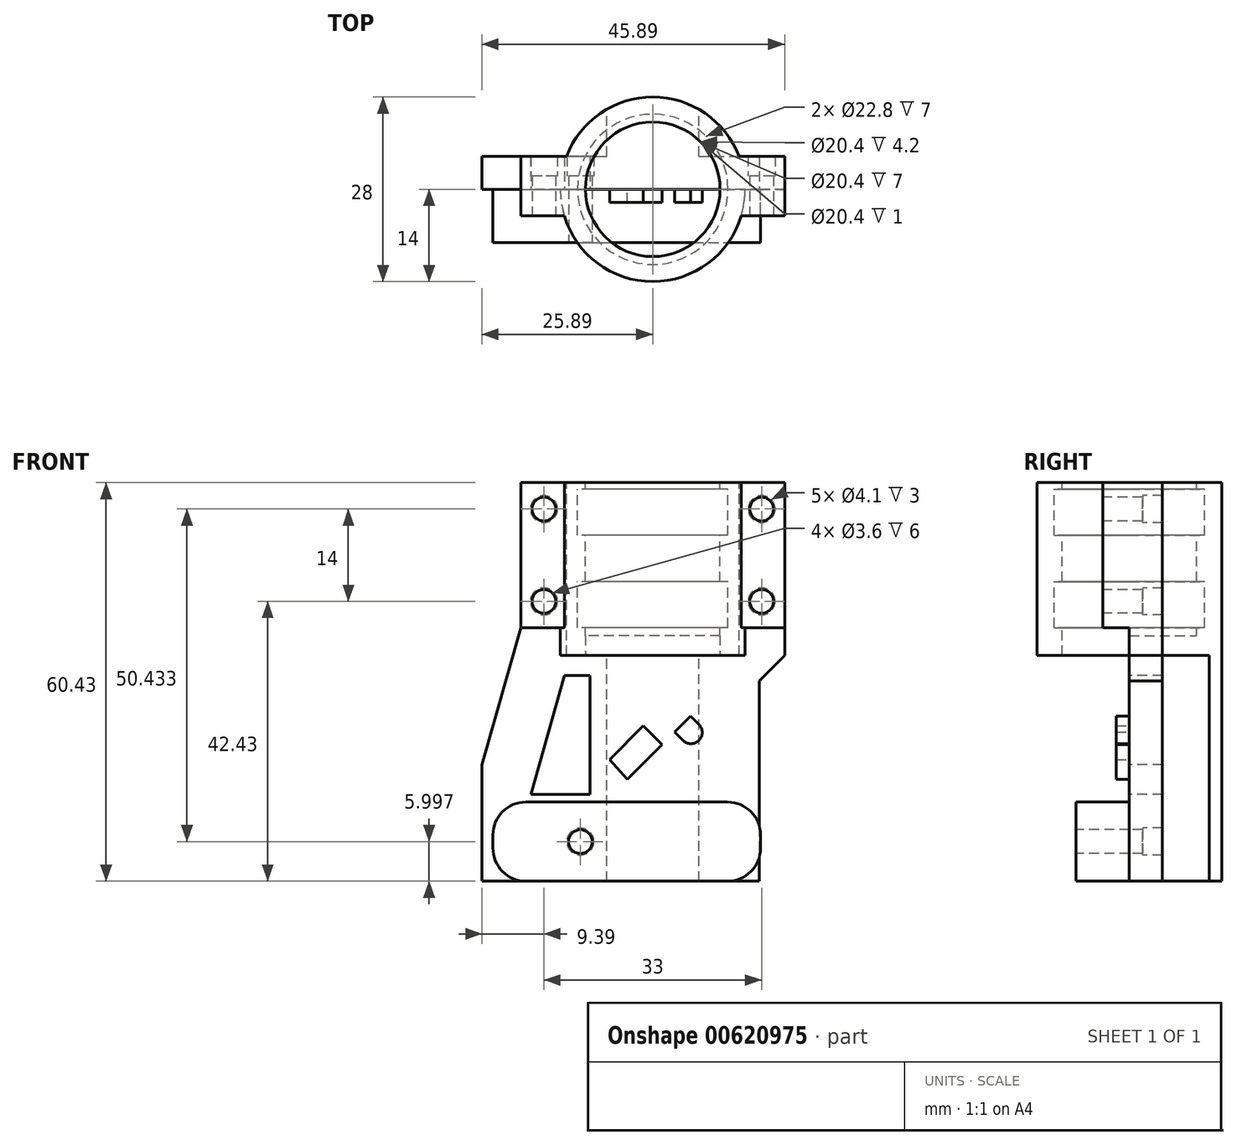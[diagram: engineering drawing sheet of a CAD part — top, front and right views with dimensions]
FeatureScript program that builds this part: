
annotation { "Feature Type Name" : "Feature", "Feature Type Description" : "" }
export const myFeature = defineFeature(function(context is Context, id is Id, definition is map)
    precondition{}
    {
        {
            var Q0;
            Q0=qCreatedBy(makeId("Front.planeOp"),FACE);
            var sketch = newSketch(context, id + "F0", { "sketchPlane" : qUnion([Q0]), "disableImprinting" : false});
            skLineSegment(sketch, "E0", {"start": v(-10.2, 21) * mm, "end": v(-11.4, 21) * mm});
            skLineSegment(sketch, "E1", {"start": v(-11.4, 21) * mm, "end": v(-11.4, 14) * mm});
            skLineSegment(sketch, "E2", {"start": v(-11.4, 14) * mm, "end": v(-10.2, 14) * mm});
            skLineSegment(sketch, "E3", {"start": v(-10.2, 14) * mm, "end": v(-10.2, 7) * mm});
            skLineSegment(sketch, "E4", {"start": v(-10.2, 7) * mm, "end": v(-11.4, 7) * mm});
            skLineSegment(sketch, "E5", {"start": v(-11.4, 7) * mm, "end": v(-11.4, 0) * mm});
            skLineSegment(sketch, "E6", {"start": v(-11.4, 0) * mm, "end": v(-10.2, 0) * mm});
            skLineSegment(sketch, "E7", {"start": v(-10.2, 0) * mm, "end": v(-10.2, -1.2) * mm});
            skLineSegment(sketch, "E8", {"start": v(-10.2, -1.2) * mm, "end": v(0, -1.2) * mm});
            skLineSegment(sketch, "E9", {"start": v(0, -1.2) * mm, "end": v(0, -4.2) * mm});
            skLineSegment(sketch, "E10", {"start": v(0, -4.2) * mm, "end": v(-14, -4.2) * mm});
            skLineSegment(sketch, "E11", {"start": v(-14, -4.2) * mm, "end": v(-14, 22) * mm});
            skLineSegment(sketch, "E12", {"start": v(-14, 22) * mm, "end": v(-10.2, 22) * mm});
            skLineSegment(sketch, "E13", {"start": v(-10.2, 22) * mm, "end": v(-10.2, 21) * mm});
            skLineSegment(sketch, "E14", {"start": v(-10.2, -1.2) * mm, "end": v(-10.2, -4.2) * mm});
            skSolve(sketch);
        }
        {
            var Q0;
            Q0=qSketchRegion(id+"F0",true);
            var Q1;
            Q1=sQuery(id+"F0.wireOp",EDGE,"E9");
            revolve(context, id + "F1", {"entities" : qUnion([Q0]), "axis" : qUnion([Q1]), "revolveType" : RevolveType.ONE_DIRECTION, "angle" : 180 * degree});
        }
        {
            var Q0;
            Q0=makeQuery(id+"F0.imprint","IMPRINT",FACE,{"disambiguationData":[TD([[makeQuery(id+"F0.imprint","IMPRINT",EDGE,{"derivedFrom":sQuery(id+"F0.wireOp",EDGE,"E0")}),-1.0]])]});
            var Q1;
            Q1=sQuery(id+"F0.wireOp",EDGE,"E9");
            revolve(context, id + "F2", {"entities" : qUnion([Q0]), "axis" : qUnion([Q1]), "revolveType" : RevolveType.ONE_DIRECTION, "oppositeDirection" : true, "angle" : 180 * degree});
        }
        {
            var Q0;
            Q0=makeQuery(id+"F1.opRevolve","CAP_FACE",FACE,{"disambiguationData":[OSD([sQuery(id+"F0.wireOp",EDGE,"E0"),sQuery(id+"F0.wireOp",EDGE,"E1"),sQuery(id+"F0.wireOp",EDGE,"E2"),sQuery(id+"F0.wireOp",EDGE,"E3"),sQuery(id+"F0.wireOp",EDGE,"E4"),sQuery(id+"F0.wireOp",EDGE,"E5"),sQuery(id+"F0.wireOp",EDGE,"E6"),sQuery(id+"F0.wireOp",EDGE,"E7"),sQuery(id+"F0.wireOp",EDGE,"E8"),sQuery(id+"F0.wireOp",EDGE,"E9"),sQuery(id+"F0.wireOp",EDGE,"E10"),sQuery(id+"F0.wireOp",EDGE,"E11"),sQuery(id+"F0.wireOp",EDGE,"E12"),sQuery(id+"F0.wireOp",EDGE,"E13")])],"isStart":false});
            var sketch = newSketch(context, id + "F3", { "sketchPlane" : qUnion([Q0])});
            skLineSegment(sketch, "E15.bottom", {"start": v(-11.4, 22) * mm, "end": v(-20, 22) * mm});
            skLineSegment(sketch, "E15.top", {"start": v(-11.4, 0) * mm, "end": v(-20, 0) * mm});
            skLineSegment(sketch, "E15.left", {"start": v(-11.4, 22) * mm, "end": v(-11.4, 0) * mm});
            skLineSegment(sketch, "E15.right", {"start": v(-20, 22) * mm, "end": v(-20, 0) * mm});
            skLineSegment(sketch, "E16", {"start": v(0, 0) * mm, "end": v(0, -4.2) * mm, "construction": true});
            skPoint(sketch, "E17", {"position": v(-16.5, 18) * mm});
            skPoint(sketch, "E17.positionSnap0", {"position": v(-16.5, 22) * mm});
            skPoint(sketch, "E18", {"position": v(-16.5, 4) * mm});
            skPoint(sketch, "E19.MirrorP", {"position": v(16.5, 4) * mm});
            skPoint(sketch, "E20.MirrorP", {"position": v(16.5, 18) * mm});
            skLineSegment(sketch, "E21.MirrorCS", {"start": v(20, 22) * mm, "end": v(20, 0) * mm});
            skLineSegment(sketch, "E22.MirrorCS", {"start": v(11.4, 22) * mm, "end": v(11.4, 0) * mm});
            skLineSegment(sketch, "E23.MirrorCS", {"start": v(11.4, 0) * mm, "end": v(20, 0) * mm});
            skLineSegment(sketch, "E24.MirrorCS", {"start": v(11.4, 22) * mm, "end": v(20, 22) * mm});
            skLineSegment(sketch, "E25.bottom", {"start": v(20, 0) * mm, "end": v(12.54, 0) * mm});
            skLineSegment(sketch, "E25.top", {"start": v(20, -4.2) * mm, "end": v(12.54, -4.2) * mm});
            skLineSegment(sketch, "E25.left", {"start": v(20, 0) * mm, "end": v(20, -4.2) * mm});
            skLineSegment(sketch, "E25.right", {"start": v(12.54, 0) * mm, "end": v(12.54, -4.2) * mm});
            skSolve(sketch);
        }
        {
            var Q0;
            Q0=qSketchRegion(id+"F3",true);
            extrude(context, id + "F4", {"entities" : qUnion([Q0]), "operationType" : NewBodyOperationType.ADD, "flatOperationType" : FlatOperationType.REMOVE, "thickness1" : 5 * mm, "thickness2" : 0 * mm, "thickness" : 5 * mm, "oppositeDirection" : true, "depth" : 5 * mm, "offsetDistance" : 25 * mm, "startOffsetBound" : StartOffsetType.BLIND, "startOffsetDistance" : 25 * mm, "domain" : OperationDomain.MODEL});
        }
        {
            var Q0;
            {var subQ3=sQuery(id+"F3.wireOp",EDGE,"E15.right");Q0=makeQuery(id+"F3.imprint","IMPRINT",FACE,{"disambiguationData":[TD([[makeQuery(id+"F3.imprint","IMPRINT",EDGE,{"derivedFrom":subQ3}),1.0]])]});}
            var Q1;
            {var subQ0=sQuery(id+"F3.wireOp",EDGE,"E21.MirrorCS");Q1=makeQuery(id+"F3.imprint","IMPRINT",FACE,{"disambiguationData":[TD([[makeQuery(id+"F3.imprint","IMPRINT",EDGE,{"derivedFrom":subQ0}),-1.0]])]});}
            var Q2;
            {var subQ0=sQuery(id+"F3.wireOp",EDGE,"E15.left");var subQ1=makeQuery(id+"F3.imprint","INTERSECT",VERTEX,{"derivedFrom":[makeQuery(id+"F1.opRevolve","CAP_EDGE",EDGE,{"disambiguationData":[OSD([sQuery(id+"F0.wireOp",EDGE,"E2")])],"isStart":true}),subQ0]});Q2=makeQuery(id+"F3.imprint","IMPRINT",FACE,{"disambiguationData":[TD([[makeQuery(id+"F3.imprint","IMPRINT",EDGE,{"disambiguationData":[TD([[subQ1,-1.0]])],"derivedFrom":subQ0}),-1.0]])]});}
            var Q3;
            {var subQ0=sQuery(id+"F3.wireOp",EDGE,"E22.MirrorCS");var subQ2=makeQuery(id+"F3.imprint","INTERSECT",VERTEX,{"derivedFrom":[makeQuery(id+"F1.opRevolve","CAP_EDGE",EDGE,{"disambiguationData":[OSD([sQuery(id+"F0.wireOp",EDGE,"E2")])],"isStart":false}),subQ0]});Q3=makeQuery(id+"F3.imprint","IMPRINT",FACE,{"disambiguationData":[TD([[makeQuery(id+"F3.imprint","IMPRINT",EDGE,{"disambiguationData":[TD([[subQ2,-1.0]])],"derivedFrom":subQ0}),1.0]])]});}
            extrude(context, id + "F5", {"entities" : qUnion([Q0, Q1, Q2, Q3]), "operationType" : NewBodyOperationType.ADD, "flatOperationType" : FlatOperationType.REMOVE, "thickness1" : 5 * mm, "thickness2" : 0 * mm, "thickness" : 5 * mm, "depth" : 4 * mm, "offsetDistance" : 25 * mm, "startOffsetBound" : StartOffsetType.BLIND, "startOffsetDistance" : 25 * mm, "domain" : OperationDomain.MODEL});
        }
        {
            var Q0;
            Q0=makeQuery(id+"F4.opExtrude","CAP_FACE",FACE,{"disambiguationData":[OSD([sQuery(id+"F3.wireOp",EDGE,"E21.MirrorCS"),sQuery(id+"F3.wireOp",EDGE,"E22.MirrorCS"),sQuery(id+"F3.wireOp",EDGE,"E23.MirrorCS"),sQuery(id+"F3.wireOp",EDGE,"E24.MirrorCS")])],"isStart":false});
            var sketch = newSketch(context, id + "F6", { "sketchPlane" : qUnion([Q0])});
            skPoint(sketch, "E26.0", {"position": v(-16.5, 18) * mm});
            skPoint(sketch, "E26.1", {"position": v(-16.5, 4) * mm});
            skPoint(sketch, "E26.2", {"position": v(16.5, 4) * mm});
            skPoint(sketch, "E26.3", {"position": v(16.5, 18) * mm});
            skSolve(sketch);
        }
        {
            var Q0;
            Q0=sQuery(id+"F6.wireOp",VERTEX,"E26.0");
            var Q1;
            Q1=sQuery(id+"F6.wireOp",VERTEX,"E26.1");
            var Q2;
            Q2=sQuery(id+"F6.wireOp",VERTEX,"E26.3");
            var Q3;
            Q3=sQuery(id+"F6.wireOp",VERTEX,"E26.2");
            var Q4;
            Q4=makeQuery(id+"F1.opRevolve","SWEPT_BODY",BODY,{"disambiguationData":[OSD([sQuery(id+"F0.wireOp",EDGE,"E0"),sQuery(id+"F0.wireOp",EDGE,"E1"),sQuery(id+"F0.wireOp",EDGE,"E2"),sQuery(id+"F0.wireOp",EDGE,"E3"),sQuery(id+"F0.wireOp",EDGE,"E4"),sQuery(id+"F0.wireOp",EDGE,"E5"),sQuery(id+"F0.wireOp",EDGE,"E6"),sQuery(id+"F0.wireOp",EDGE,"E7"),sQuery(id+"F0.wireOp",EDGE,"E8"),sQuery(id+"F0.wireOp",EDGE,"E9"),sQuery(id+"F0.wireOp",EDGE,"E10"),sQuery(id+"F0.wireOp",EDGE,"E11"),sQuery(id+"F0.wireOp",EDGE,"E12"),sQuery(id+"F0.wireOp",EDGE,"E13")])]});
            var Q5;
            Q5=makeQuery(id+"F2.opRevolve","SWEPT_BODY",BODY,{"disambiguationData":[OSD([sQuery(id+"F0.wireOp",EDGE,"E0"),sQuery(id+"F0.wireOp",EDGE,"E1"),sQuery(id+"F0.wireOp",EDGE,"E2"),sQuery(id+"F0.wireOp",EDGE,"E3"),sQuery(id+"F0.wireOp",EDGE,"E4"),sQuery(id+"F0.wireOp",EDGE,"E5"),sQuery(id+"F0.wireOp",EDGE,"E6"),sQuery(id+"F0.wireOp",EDGE,"E7"),sQuery(id+"F0.wireOp",EDGE,"E8"),sQuery(id+"F0.wireOp",EDGE,"E9"),sQuery(id+"F0.wireOp",EDGE,"E10"),sQuery(id+"F0.wireOp",EDGE,"E11"),sQuery(id+"F0.wireOp",EDGE,"E12"),sQuery(id+"F0.wireOp",EDGE,"E13")])]});
            hole(context, id + "F7", {"style" : HoleStyle.C_BORE, "endStyle" : HoleEndStyle.THROUGH, "holeDiameter" : 3.6 * mm, "cBoreDiameter" : 4.1 * mm, "cBoreDepth" : 3 * mm, "majorDiameter" : 5 * mm, "isTappedThrough" : true, "tappedDepth" : 7 * mm, "tapClearance" : 6, "locations" : qUnion([Q0, Q1, Q2, Q3]), "scope" : qUnion([Q4, Q5]), "startStyle" : HoleStartStyle.SKETCH});
        }
        {
            var Q0;
            Q0=qCreatedBy(makeId("Front.planeOp"),FACE);
            var sketch = newSketch(context, id + "F8", { "sketchPlane" : qUnion([Q0])});
            skLineSegment(sketch, "E27", {"start": v(0, 7.53) * mm, "end": v(0, -50) * mm, "construction": true});
            skLineSegment(sketch, "E28", {"start": v(-3.83, -22.95) * mm, "end": v(17.38, -1.74) * mm, "construction": true});
            skLineSegment(sketch, "E29", {"start": v(-1, -47) * mm, "end": v(41.43, -4.56) * mm, "construction": true});
            skLineSegment(sketch, "E30", {"start": v(20.21, -25.78) * mm, "end": v(5.8, -11.37) * mm, "construction": true});
            skLineSegment(sketch, "E31", {"start": v(17.38, -1.74) * mm, "end": v(41.43, -4.56) * mm, "construction": true});
            skLineSegment(sketch, "E32", {"start": v(-3.83, -22.95) * mm, "end": v(-1, -47) * mm, "construction": true});
            skLineSegment(sketch, "E33", {"start": v(5.72, -13.4) * mm, "end": v(7, -14.68) * mm, "construction": true});
            skLineSegment(sketch, "E34", {"start": v(3.31, -15.8) * mm, "end": v(4.59, -17.08) * mm, "construction": true});
            skArc(sketch, "E35", {"start": v(4.59, -17.08) * mm, "mid": v(7, -17.08) * mm, "end": v(7, -14.68) * mm});
            skPoint(sketch, "E36", {"position": v(7, -17.08) * mm});
            skSolve(sketch);
        }
        {
            var Q0;
            Q0=makeQuery(id+"F0.imprint","IMPRINT",FACE,{"disambiguationData":[TD([[makeQuery(id+"F0.imprint","IMPRINT",EDGE,{"derivedFrom":sQuery(id+"F0.wireOp",EDGE,"E0")}),-1.0]])]});
            var sketch = newSketch(context, id + "F9", { "sketchPlane" : qUnion([Q0])});
            skLineSegment(sketch, "E37.top", {"start": v(-25.9, -38.43) * mm, "end": v(16.16, -38.43) * mm});
            skLineSegment(sketch, "E37.left", {"start": v(-25.9, -20.76) * mm, "end": v(-25.9, -38.43) * mm});
            skLineSegment(sketch, "E37.right", {"start": v(16.16, -8.04) * mm, "end": v(16.16, -38.43) * mm});
            skArc(sketch, "E38.0", {"start": v(4.59, -17.08) * mm, "mid": v(7, -17.08) * mm, "end": v(7, -14.68) * mm});
            skLineSegment(sketch, "E38.1", {"start": v(3.31, -15.8) * mm, "end": v(4.59, -17.08) * mm});
            skLineSegment(sketch, "E38.2", {"start": v(5.72, -13.4) * mm, "end": v(7, -14.68) * mm});
            skLineSegment(sketch, "E38.3", {"start": v(-3.83, -22.95) * mm, "end": v(1.4, -17.72) * mm});
            skLineSegment(sketch, "E39", {"start": v(-3.85, -22.97) * mm, "end": v(1.4, -17.72) * mm});
            skLineSegment(sketch, "E40", {"start": v(1.4, -17.72) * mm, "end": v(-1.42, -14.89) * mm});
            skLineSegment(sketch, "E41", {"start": v(-1.42, -14.89) * mm, "end": v(-6.53, -20) * mm});
            skLineSegment(sketch, "E42", {"start": v(-6.53, -20) * mm, "end": v(-3.85, -22.97) * mm});
            skLineSegment(sketch, "E43", {"start": v(-20, 0) * mm, "end": v(-25.9, -20.76) * mm});
            skLineSegment(sketch, "E44", {"start": v(-9.49, -7.27) * mm, "end": v(-9.49, -25.26) * mm});
            skLineSegment(sketch, "E45", {"start": v(-9.49, -25.26) * mm, "end": v(-18.46, -25.26) * mm});
            skLineSegment(sketch, "E46", {"start": v(-18.46, -25.26) * mm, "end": v(-13.36, -7.27) * mm});
            skPoint(sketch, "E47.0", {"position": v(-20, 0) * mm});
            skLineSegment(sketch, "E48", {"start": v(-13.36, -7.27) * mm, "end": v(-9.49, -7.27) * mm});
            skLineSegment(sketch, "E49", {"start": v(20, -4.2) * mm, "end": v(16.16, -8.04) * mm});
            skPoint(sketch, "E50.orphan", {"position": v(17.38, -1.74) * mm});
            skLineSegment(sketch, "E51.trimOffspring", {"start": v(3.31, -15.8) * mm, "end": v(5.72, -13.4) * mm});
            skLineSegment(sketch, "E52", {"start": v(20, -4.2) * mm, "end": v(-10.89, -4.2) * mm});
            skLineSegment(sketch, "E53", {"start": v(-10.89, -4.2) * mm, "end": v(-10.89, 0) * mm});
            skLineSegment(sketch, "E54", {"start": v(-10.89, 0) * mm, "end": v(-20, 0) * mm});
            skSolve(sketch);
        }
        {
            var Q0;
            {var subQ5=sQuery(id+"F9.wireOp",EDGE,"E53");Q0=makeQuery(id+"F9.imprint","IMPRINT",FACE,{"disambiguationData":[TD([[makeQuery(id+"F9.imprint","IMPRINT",EDGE,{"derivedFrom":subQ5}),1.0]])]});}
            var Q1;
            Q1=makeQuery(id+"F9.imprint","IMPRINT",FACE,{"disambiguationData":[TD([[makeQuery(id+"F9.imprint","IMPRINT",EDGE,{"derivedFrom":sQuery(id+"F9.wireOp",EDGE,"E37.top")}),1.0]])]});
            var Q2;
            Q2=makeQuery(id+"F9.imprint","IMPRINT",FACE,{"disambiguationData":[TD([[makeQuery(id+"F9.imprint","IMPRINT",EDGE,{"derivedFrom":sQuery(id+"F9.wireOp",EDGE,"E38.0")}),1.0]])]});
            var Q3;
            {var subQ0=sQuery(id+"F9.wireOp",EDGE,"E40");Q3=makeQuery(id+"F9.imprint","IMPRINT",FACE,{"disambiguationData":[TD([[makeQuery(id+"F9.imprint","IMPRINT",EDGE,{"derivedFrom":subQ0}),1.0]])]});}
            extrude(context, id + "F10", {"entities" : qUnion([Q0, Q1, Q2, Q3]), "operationType" : NewBodyOperationType.ADD, "thickness1" : 5 * mm, "thickness2" : 0 * mm, "thickness" : 5 * mm, "oppositeDirection" : true, "depth" : 5 * mm, "offsetDistance" : 25 * mm, "startOffsetBound" : StartOffsetType.BLIND, "startOffsetDistance" : 25 * mm, "flatOperationType" : FlatOperationType.REMOVE, "domain" : OperationDomain.MODEL});
        }
        {
            var Q0;
            Q0=makeQuery(id+"F9.imprint","IMPRINT",FACE,{"disambiguationData":[TD([[makeQuery(id+"F9.imprint","IMPRINT",EDGE,{"derivedFrom":sQuery(id+"F9.wireOp",EDGE,"E39")}),1.0]])]});
            var Q1;
            Q1=makeQuery(id+"F9.imprint","IMPRINT",FACE,{"disambiguationData":[TD([[makeQuery(id+"F9.imprint","IMPRINT",EDGE,{"derivedFrom":sQuery(id+"F9.wireOp",EDGE,"E38.0")}),1.0]])]});
            extrude(context, id + "F11", {"entities" : qUnion([Q0, Q1]), "operationType" : NewBodyOperationType.ADD, "depth" : 2 * mm, "offsetDistance" : 25 * mm});
        }
        {
            var Q0;
            Q0=makeQuery(id+"F10.boolean.opBoolean","MERGE",FACE,{"derivedFrom":[makeQuery(id+"F4.boolean.opBoolean","MERGE",FACE,{"derivedFrom":[makeQuery(id+"F1.opRevolve","CAP_FACE",FACE,{"disambiguationData":[OSD([sQuery(id+"F0.wireOp",EDGE,"E0"),sQuery(id+"F0.wireOp",EDGE,"E1"),sQuery(id+"F0.wireOp",EDGE,"E2"),sQuery(id+"F0.wireOp",EDGE,"E3"),sQuery(id+"F0.wireOp",EDGE,"E4"),sQuery(id+"F0.wireOp",EDGE,"E5"),sQuery(id+"F0.wireOp",EDGE,"E6"),sQuery(id+"F0.wireOp",EDGE,"E7"),sQuery(id+"F0.wireOp",EDGE,"E8"),sQuery(id+"F0.wireOp",EDGE,"E9"),sQuery(id+"F0.wireOp",EDGE,"E10"),sQuery(id+"F0.wireOp",EDGE,"E11"),sQuery(id+"F0.wireOp",EDGE,"E12"),sQuery(id+"F0.wireOp",EDGE,"E13")])],"isStart":false}),makeQuery(id+"F4.opExtrude","CAP_FACE",FACE,{"disambiguationData":[OSD([sQuery(id+"F3.wireOp",EDGE,"E15.bottom"),sQuery(id+"F3.wireOp",EDGE,"E15.top"),sQuery(id+"F3.wireOp",EDGE,"E15.left"),sQuery(id+"F3.wireOp",EDGE,"E15.right")])],"isStart":true}),makeQuery(id+"F4.opExtrude","CAP_FACE",FACE,{"disambiguationData":[OSD([sQuery(id+"F3.wireOp",EDGE,"E21.MirrorCS"),sQuery(id+"F3.wireOp",EDGE,"E22.MirrorCS"),sQuery(id+"F3.wireOp",EDGE,"E23.MirrorCS"),sQuery(id+"F3.wireOp",EDGE,"E24.MirrorCS")])],"isStart":true})]}),makeQuery(id+"F10.opExtrude","CAP_FACE",FACE,{"disambiguationData":[OSD([sQuery(id+"F9.wireOp",EDGE,"E37.top"),sQuery(id+"F9.wireOp",EDGE,"E37.left"),sQuery(id+"F9.wireOp",EDGE,"E37.right"),sQuery(id+"F9.wireOp",EDGE,"sIr9ozcs-yVTk-N2fr-iWXJ-KNAt2VVmV1aQ")])],"isStart":true})]});
            var sketch = newSketch(context, id + "F12", { "sketchPlane" : qUnion([Q0]), "disableImprinting" : false});
            skLineSegment(sketch, "E55.bottom", {"start": v(-24.23, -26.43) * mm, "end": v(16.34, -26.43) * mm});
            skLineSegment(sketch, "E55.top", {"start": v(-24.23, -38.43) * mm, "end": v(16.34, -38.43) * mm});
            skLineSegment(sketch, "E55.left", {"start": v(-24.23, -26.43) * mm, "end": v(-24.23, -38.43) * mm});
            skLineSegment(sketch, "E55.right", {"start": v(16.34, -26.43) * mm, "end": v(16.34, -38.43) * mm});
            skPoint(sketch, "E56", {"position": v(-10.97, -32.43) * mm});
            skPoint(sketch, "E56.positionSnap0", {"position": v(-24.23, -32.43) * mm});
            skSolve(sketch);
        }
        {
            var Q0;
            Q0=makeQuery(id+"F12.imprint","IMPRINT",FACE,{"disambiguationData":[TD([[makeQuery(id+"F12.imprint","IMPRINT",EDGE,{"derivedFrom":sQuery(id+"F12.wireOp",EDGE,"E55.bottom")}),-1.0]])]});
            extrude(context, id + "F13", {"entities" : qUnion([Q0]), "depth" : 8.1 * mm, "offsetDistance" : 25 * mm});
        }
        {
            var Q0;
            Q0=makeQuery(id+"F10.boolean.opBoolean","MERGE",FACE,{"derivedFrom":[makeQuery(id+"F4.opExtrude","CAP_FACE",FACE,{"disambiguationData":[OSD([sQuery(id+"F3.wireOp",EDGE,"E21.MirrorCS"),sQuery(id+"F3.wireOp",EDGE,"E22.MirrorCS"),sQuery(id+"F3.wireOp",EDGE,"E23.MirrorCS"),sQuery(id+"F3.wireOp",EDGE,"E24.MirrorCS"),sQuery(id+"F3.wireOp",EDGE,"E25.top"),sQuery(id+"F3.wireOp",EDGE,"E25.left"),sQuery(id+"F3.wireOp",EDGE,"E25.right")])],"isStart":false}),makeQuery(id+"F4.opExtrude","CAP_FACE",FACE,{"disambiguationData":[OSD([sQuery(id+"F3.wireOp",EDGE,"E15.bottom"),sQuery(id+"F3.wireOp",EDGE,"E15.top"),sQuery(id+"F3.wireOp",EDGE,"E15.left"),sQuery(id+"F3.wireOp",EDGE,"E15.right")])],"isStart":false}),makeQuery(id+"F10.opExtrude","CAP_FACE",FACE,{"disambiguationData":[OSD([sQuery(id+"F9.wireOp",EDGE,"E37.top"),sQuery(id+"F9.wireOp",EDGE,"E37.left"),sQuery(id+"F9.wireOp",EDGE,"E37.right"),sQuery(id+"F9.wireOp",EDGE,"E43"),sQuery(id+"F9.wireOp",EDGE,"E44"),sQuery(id+"F9.wireOp",EDGE,"E45"),sQuery(id+"F9.wireOp",EDGE,"E46"),sQuery(id+"F9.wireOp",EDGE,"E48"),sQuery(id+"F9.wireOp",EDGE,"E49"),sQuery(id+"F9.wireOp",EDGE,"E52"),sQuery(id+"F9.wireOp",EDGE,"E53"),sQuery(id+"F9.wireOp",EDGE,"E54")])],"isStart":false})]});
            var sketch = newSketch(context, id + "F14", { "sketchPlane" : qUnion([Q0]), "disableImprinting" : false});
            skPoint(sketch, "E57.0", {"position": v(10.97, -32.43) * mm});
            skSolve(sketch);
        }
        {
            var Q0;
            Q0=sQuery(id+"F14.wireOp",VERTEX,"E57.0");
            var Q1;
            Q1=makeQuery(id+"F13.opExtrude","SWEPT_BODY",BODY,{"disambiguationData":[OSD([sQuery(id+"F12.wireOp",EDGE,"E55.bottom"),sQuery(id+"F12.wireOp",EDGE,"E55.top"),sQuery(id+"F12.wireOp",EDGE,"E55.left"),sQuery(id+"F12.wireOp",EDGE,"E55.right")])]});
            var Q2;
            Q2=makeQuery(id+"F1.opRevolve","SWEPT_BODY",BODY,{"disambiguationData":[OSD([sQuery(id+"F0.wireOp",EDGE,"E0"),sQuery(id+"F0.wireOp",EDGE,"E1"),sQuery(id+"F0.wireOp",EDGE,"E2"),sQuery(id+"F0.wireOp",EDGE,"E3"),sQuery(id+"F0.wireOp",EDGE,"E4"),sQuery(id+"F0.wireOp",EDGE,"E5"),sQuery(id+"F0.wireOp",EDGE,"E6"),sQuery(id+"F0.wireOp",EDGE,"E7"),sQuery(id+"F0.wireOp",EDGE,"E8"),sQuery(id+"F0.wireOp",EDGE,"E9"),sQuery(id+"F0.wireOp",EDGE,"E10"),sQuery(id+"F0.wireOp",EDGE,"E11"),sQuery(id+"F0.wireOp",EDGE,"E12"),sQuery(id+"F0.wireOp",EDGE,"E13")])]});
            hole(context, id + "F15", {"style" : HoleStyle.C_BORE, "endStyle" : HoleEndStyle.THROUGH, "offsetDistance" : 5 * mm, "threadStandard" : ThreadStandard.UNSET, "ansiThreadClass" : lookupTablePath({ "class" : "2B" }), "isoThreadClass" : lookupTablePath({ "class" : "6H" }), "holeDiameter" : 3.6 * mm, "holeDiameterToleranceType" : ToleranceTypeExtended.NONE, "holeDiameterToleranceBoundSymmetrical" : 0.1 * mm, "holeDiameterToleranceBoundDeviationUpper" : 0.1 * mm, "holeDiameterToleranceBoundDeviationLower" : -0.1 * mm, "holeDiameterToleranceBoundLimitsUpper" : 0.1 * mm, "holeDiameterToleranceBoundLimitsLower" : -0.1 * mm, "holeDiameterFitToleranceTable" : lookupTablePath({ "fit" : "User defined", "standard" : "ISO", "shaftClass" : "None", "holeClass" : "A9" }), "holeDiameterholeClassToleranceBoundLimitsUpper" : 0.1 * mm, "holeDiameterholeClassToleranceBoundLimitsLower" : -0.1 * mm, "cBoreDiameter" : 4.1 * mm, "cBoreDiameterToleranceType" : ToleranceType.NONE, "cBoreDiameterToleranceBoundSymmetrical" : 0.1 * mm, "cBoreDiameterToleranceBoundDeviationUpper" : 0.1 * mm, "cBoreDiameterToleranceBoundDeviationLower" : -0.1 * mm, "cBoreDiameterToleranceBoundLimitsUpper" : 0.1 * mm, "cBoreDiameterToleranceBoundLimitsLower" : -0.1 * mm, "cBoreDepth" : 3 * mm, "cBoreDepthToleranceType" : ToleranceType.NONE, "cBoreDepthToleranceBoundSymmetrical" : 0.1 * mm, "cBoreDepthToleranceBoundDeviationUpper" : 0.1 * mm, "cBoreDepthToleranceBoundDeviationLower" : -0.1 * mm, "cBoreDepthToleranceBoundLimitsUpper" : 0.1 * mm, "cBoreDepthToleranceBoundLimitsLower" : -0.1 * mm, "cSinkDiameterToleranceType" : ToleranceType.NONE, "cSinkDiameterToleranceBoundSymmetrical" : 0.1 * mm, "cSinkDiameterToleranceBoundDeviationUpper" : 0.1 * mm, "cSinkDiameterToleranceBoundDeviationLower" : -0.1 * mm, "cSinkDiameterToleranceBoundLimitsUpper" : 0.1 * mm, "cSinkDiameterToleranceBoundLimitsLower" : -0.1 * mm, "cSinkAngleToleranceType" : ToleranceType.NONE, "cSinkAngleToleranceBoundSymmetrical" : 1 * degree, "cSinkAngleToleranceBoundDeviationUpper" : 1 * degree, "cSinkAngleToleranceBoundDeviationLower" : -1 * degree, "cSinkAngleToleranceBoundLimitsUpper" : 1 * degree, "cSinkAngleToleranceBoundLimitsLower" : -1 * degree, "tapDrillDiameterToleranceType" : ToleranceType.NONE, "tapDrillDiameterToleranceBoundSymmetrical" : 0.1 * mm, "tapDrillDiameterToleranceBoundDeviationUpper" : 0.1 * mm, "tapDrillDiameterToleranceBoundDeviationLower" : -0.1 * mm, "tapDrillDiameterToleranceBoundLimitsUpper" : 0.1 * mm, "tapDrillDiameterToleranceBoundLimitsLower" : -0.1 * mm, "majorDiameter" : 5 * mm, "holeDepthMultiple" : "Multiple", "holeDepthMultipleToleranceType" : ToleranceType.NONE, "holeDepthMultipleToleranceBoundSymmetrical" : 0.1 * mm, "holeDepthMultipleToleranceBoundDeviationUpper" : 0.1 * mm, "holeDepthMultipleToleranceBoundDeviationLower" : -0.1 * mm, "holeDepthMultipleToleranceBoundLimitsUpper" : 0.1 * mm, "holeDepthMultipleToleranceBoundLimitsLower" : -0.1 * mm, "holeDepthComputed" : 12 * mm, "holeDepthComputedToleranceType" : ToleranceType.NONE, "holeDepthComputedToleranceBoundSymmetrical" : 0.1 * mm, "holeDepthComputedToleranceBoundDeviationUpper" : 0.1 * mm, "holeDepthComputedToleranceBoundDeviationLower" : -0.1 * mm, "holeDepthComputedToleranceBoundLimitsUpper" : 0.1 * mm, "holeDepthComputedToleranceBoundLimitsLower" : -0.1 * mm, "holeDepthToleranceType" : ToleranceType.NONE, "holeDepthToleranceBoundSymmetrical" : 0.1 * mm, "holeDepthToleranceBoundDeviationUpper" : 0.1 * mm, "holeDepthToleranceBoundDeviationLower" : -0.1 * mm, "holeDepthToleranceBoundLimitsUpper" : 0.1 * mm, "holeDepthToleranceBoundLimitsLower" : -0.1 * mm, "tipAngleStyle" : TipAngleStyle.DEGREE118, "tipAngle" : 118 * degree, "tipAngleToleranceType" : ToleranceType.NONE, "tipAngleToleranceBoundSymmetrical" : 1 * degree, "tipAngleToleranceBoundDeviationUpper" : 1 * degree, "tipAngleToleranceBoundDeviationLower" : -1 * degree, "tipAngleToleranceBoundLimitsUpper" : 1 * degree, "tipAngleToleranceBoundLimitsLower" : -1 * degree, "isTappedThrough" : true, "tappedDepth" : 7 * mm, "tappedDepthToleranceType" : ToleranceType.NONE, "tappedDepthToleranceBoundSymmetrical" : 0.1 * mm, "tappedDepthToleranceBoundDeviationUpper" : 0.1 * mm, "tappedDepthToleranceBoundDeviationLower" : -0.1 * mm, "tappedDepthToleranceBoundLimitsUpper" : 0.1 * mm, "tappedDepthToleranceBoundLimitsLower" : -0.1 * mm, "tappedAngle" : 1.79 * degree, "tapClearance" : 6, "locations" : qUnion([Q0]), "scope" : qUnion([Q1, Q2]), "startStyle" : HoleStartStyle.SKETCH, "featureName" : "Ø #holeDiameter THRU | ⌴Ø #cBoreDiameter ↧ #cBoreDepth"});
        }
        {
            var Q0;
            {var subQ0=sQuery(id+"F3.wireOp",EDGE,"E25.top");Q0=makeQuery(id+"F10.boolean.opBoolean","SPLIT",FACE,{"disambiguationData":[TD([makeQuery(id+"F1.opRevolve","SWEPT_FACE",FACE,{"disambiguationData":[OSD([sQuery(id+"F0.wireOp",EDGE,"E11")])]})])],"derivedFrom":makeQuery(id+"F4.boolean.opBoolean","MERGE",FACE,{"derivedFrom":[makeQuery(id+"F1.opRevolve","SWEPT_FACE",FACE,{"disambiguationData":[OSD([sQuery(id+"F0.wireOp",EDGE,"E10")])]}),makeQuery(id+"F4.opExtrude","SWEPT_FACE",FACE,{"disambiguationData":[OSD([subQ0])]})]})});}
            var sketch = newSketch(context, id + "F16", { "sketchPlane" : qUnion([Q0])});
            skLineSegment(sketch, "E58", {"start": v(-7, -5) * mm, "end": v(-7, -12.12) * mm});
            skLineSegment(sketch, "E59", {"start": v(7, -5) * mm, "end": v(7, -12.12) * mm});
            skLineSegment(sketch, "E60", {"start": v(0, -18.83) * mm, "end": v(0, 16.75) * mm, "construction": true});
            skSolve(sketch);
        }
        {
            var Q0;
            {var subQ0=sQuery(id+"F16.wireOp",EDGE,"E58");Q0=makeQuery(id+"F16.imprint","IMPRINT",FACE,{"disambiguationData":[TD([[makeQuery(id+"F16.imprint","IMPRINT",EDGE,{"derivedFrom":subQ0}),1.0]])]});}
            var Q1;
            {var subQ0=sQuery(id+"F9.wireOp",EDGE,"E37.top");Q1=makeQuery(id+"FdEIk58ueYuawqO_3.boolean.opBoolean","MERGE",FACE,{"derivedFrom":[makeQuery(id+"F10.opExtrude","SWEPT_FACE",FACE,{"disambiguationData":[OSD([subQ0])]}),makeQuery(id+"FdEIk58ueYuawqO_3.opExtrude","CAP_FACE",FACE,{"disambiguationData":[OSD([subQ0])],"isStart":false})]});}
            extrude(context, id + "F17", {"entities" : qUnion([Q0]), "operationType" : NewBodyOperationType.ADD, "endBound" : BoundingType.UP_TO_SURFACE, "depth" : 25 * mm, "endBoundEntityFace" : qUnion([Q1]), "offsetDistance" : 25 * mm});
        }
        {
            var Q0;
            Q0=makeQuery(id+"F13.opExtrude","SWEPT_EDGE",EDGE,{"disambiguationData":[OSD([sQuery(id+"F12.wireOp",EDGE,"E55.bottom"),sQuery(id+"F12.wireOp",EDGE,"E55.left")])]});
            var Q1;
            Q1=makeQuery(id+"F13.opExtrude","SWEPT_EDGE",EDGE,{"disambiguationData":[OSD([sQuery(id+"F9.wireOp",EDGE,"E37.top"),sQuery(id+"F12.wireOp",EDGE,"E55.top"),sQuery(id+"F12.wireOp",EDGE,"E55.left")])]});
            var Q2;
            Q2=makeQuery(id+"F13.opExtrude","SWEPT_EDGE",EDGE,{"disambiguationData":[OSD([sQuery(id+"F12.wireOp",EDGE,"E55.top"),sQuery(id+"F12.wireOp",EDGE,"E55.right")])]});
            var Q3;
            Q3=makeQuery(id+"F13.opExtrude","SWEPT_EDGE",EDGE,{"disambiguationData":[OSD([sQuery(id+"F12.wireOp",EDGE,"E55.bottom"),sQuery(id+"F12.wireOp",EDGE,"E55.right")])]});
            fillet(context, id + "F18", {"entities" : qUnion([Q0, Q1, Q2, Q3]), "radius" : 5 * mm, "tangentPropagation" : true, "allowEdgeOverflow" : false});
        }
    });
